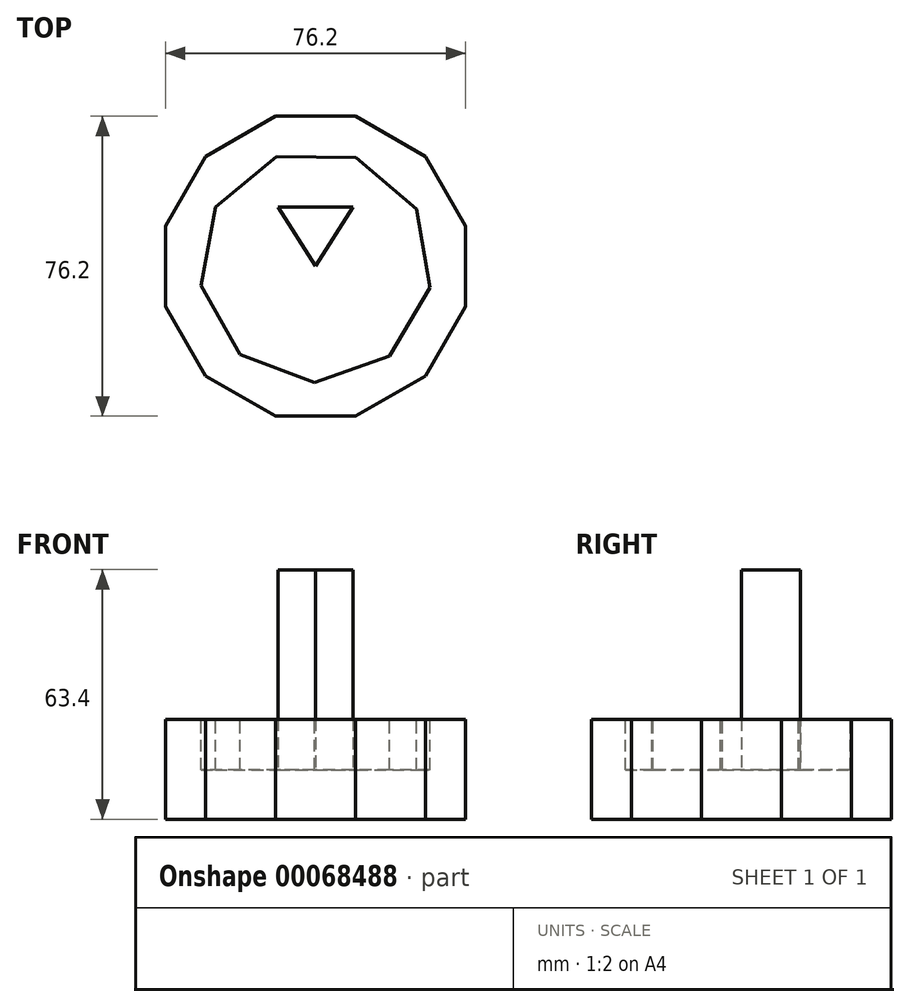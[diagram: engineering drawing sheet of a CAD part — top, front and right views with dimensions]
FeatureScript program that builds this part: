
annotation { "Feature Type Name" : "Feature", "Feature Type Description" : "" }
export const myFeature = defineFeature(function(context is Context, id is Id, definition is map)
    precondition{}
    {
        {
            var Q0;
            Q0=qCreatedBy(makeId("Top.planeOp"),FACE);
            var sketch = newSketch(context, id + "F0", { "sketchPlane" : qUnion([Q0])});
            skCircle(sketch, "E0.cCircle", {"center": v(0, 0) * mm, "radius": 38.1 * mm, "construction": true});
            skLineSegment(sketch, "E0.0", {"start": v(38.1, 10.2) * mm, "end": v(38.1, -10.2) * mm});
            skLineSegment(sketch, "E0.1", {"start": v(38.1, -10.2) * mm, "end": v(27.9, -27.9) * mm});
            skLineSegment(sketch, "E0.2", {"start": v(27.9, -27.9) * mm, "end": v(10.2, -38.1) * mm});
            skLineSegment(sketch, "E0.3", {"start": v(10.2, -38.1) * mm, "end": v(-10.2, -38.1) * mm});
            skLineSegment(sketch, "E0.4", {"start": v(-10.2, -38.1) * mm, "end": v(-27.9, -27.9) * mm});
            skLineSegment(sketch, "E0.5", {"start": v(-27.9, -27.9) * mm, "end": v(-38.1, -10.2) * mm});
            skLineSegment(sketch, "E0.6", {"start": v(-38.1, -10.2) * mm, "end": v(-38.1, 10.2) * mm});
            skLineSegment(sketch, "E0.7", {"start": v(-38.1, 10.2) * mm, "end": v(-27.9, 27.9) * mm});
            skLineSegment(sketch, "E0.8", {"start": v(-27.9, 27.9) * mm, "end": v(-10.2, 38.1) * mm});
            skLineSegment(sketch, "E0.9", {"start": v(-10.2, 38.1) * mm, "end": v(10.2, 38.1) * mm});
            skLineSegment(sketch, "E0.10", {"start": v(10.2, 38.1) * mm, "end": v(27.9, 27.9) * mm});
            skLineSegment(sketch, "E0.11", {"start": v(27.9, 27.9) * mm, "end": v(38.1, 10.2) * mm});
            skPoint(sketch, "E0.0.midPoint", {"position": v(38.1, 0) * mm});
            skSolve(sketch);
        }
        {
            var Q0;
            Q0 = qSketchRegion(id + "F0", true);
            extrude(context, id + "F1", {"entities" : qUnion([Q0]), "depth" : 25.4 * mm});
        }
        {
            var Q0;
            Q0=makeQuery(id+"F1.opExtrude","CAP_FACE",FACE,{"disambiguationData":[OSD([sQuery(id+"F0.wireOp",EDGE,"E0.0"),sQuery(id+"F0.wireOp",EDGE,"E0.1"),sQuery(id+"F0.wireOp",EDGE,"E0.2"),sQuery(id+"F0.wireOp",EDGE,"E0.3"),sQuery(id+"F0.wireOp",EDGE,"E0.4"),sQuery(id+"F0.wireOp",EDGE,"E0.5"),sQuery(id+"F0.wireOp",EDGE,"E0.6"),sQuery(id+"F0.wireOp",EDGE,"E0.7"),sQuery(id+"F0.wireOp",EDGE,"E0.8"),sQuery(id+"F0.wireOp",EDGE,"E0.9"),sQuery(id+"F0.wireOp",EDGE,"E0.10"),sQuery(id+"F0.wireOp",EDGE,"E0.11")])],"isStart":false});
            var sketch = newSketch(context, id + "F2", { "sketchPlane" : qUnion([Q0])});
            skCircle(sketch, "E1.cCircle", {"center": v(0, 0) * mm, "radius": 27.74 * mm, "construction": true});
            skLineSegment(sketch, "E1.0", {"start": v(29.03, -5.37) * mm, "end": v(18.79, -22.78) * mm});
            skLineSegment(sketch, "E1.1", {"start": v(18.79, -22.78) * mm, "end": v(-0.25, -29.52) * mm});
            skLineSegment(sketch, "E1.2", {"start": v(-0.25, -29.52) * mm, "end": v(-19.17, -22.46) * mm});
            skLineSegment(sketch, "E1.3", {"start": v(-19.17, -22.46) * mm, "end": v(-29.12, -4.88) * mm});
            skLineSegment(sketch, "E1.4", {"start": v(-29.12, -4.88) * mm, "end": v(-25.44, 14.98) * mm});
            skLineSegment(sketch, "E1.5", {"start": v(-25.44, 14.98) * mm, "end": v(-9.86, 27.83) * mm});
            skLineSegment(sketch, "E1.6", {"start": v(-9.86, 27.83) * mm, "end": v(10.33, 27.66) * mm});
            skLineSegment(sketch, "E1.7", {"start": v(10.33, 27.66) * mm, "end": v(25.7, 14.55) * mm});
            skLineSegment(sketch, "E1.8", {"start": v(25.7, 14.55) * mm, "end": v(29.03, -5.37) * mm});
            skPoint(sketch, "E1.0.midPoint", {"position": v(23.9, -14.07) * mm});
            skSolve(sketch);
        }
        {
            var Q0;
            Q0=makeQuery(id+"F2.imprint","IMPRINT",FACE,{"disambiguationData":[TD([[makeQuery(id+"F2.imprint","IMPRINT",EDGE,{"derivedFrom":sQuery(id+"F2.wireOp",EDGE,"E1.0")}),-1.0]])]});
            extrude(context, id + "F3", {"entities" : qUnion([Q0]), "operationType" : NewBodyOperationType.REMOVE, "oppositeDirection" : true, "depth" : 12.8 * mm});
        }
        {
            var Q0;
            Q0=makeQuery(id+"F3.boolean.opBoolean","COPY",FACE,{"derivedFrom":makeQuery(id+"F3.opExtrude","CAP_FACE",FACE,{"disambiguationData":[OSD([sQuery(id+"F2.wireOp",EDGE,"E1.0"),sQuery(id+"F2.wireOp",EDGE,"E1.1"),sQuery(id+"F2.wireOp",EDGE,"E1.2"),sQuery(id+"F2.wireOp",EDGE,"E1.3"),sQuery(id+"F2.wireOp",EDGE,"E1.4"),sQuery(id+"F2.wireOp",EDGE,"E1.5"),sQuery(id+"F2.wireOp",EDGE,"E1.6"),sQuery(id+"F2.wireOp",EDGE,"E1.7"),sQuery(id+"F2.wireOp",EDGE,"E1.8")])],"isStart":false})});
            var sketch = newSketch(context, id + "F4", { "sketchPlane" : qUnion([Q0])});
            skLineSegment(sketch, "E2", {"start": v(0, 0) * mm, "end": v(9.54, 14.98) * mm});
            skLineSegment(sketch, "E3", {"start": v(9.54, 14.98) * mm, "end": v(-9.54, 14.98) * mm});
            skLineSegment(sketch, "E4", {"start": v(-9.54, 14.98) * mm, "end": v(0, 0) * mm});
            skSolve(sketch);
        }
        {
            var Q0;
            Q0 = qSketchRegion(id + "F4", true);
            extrude(context, id + "F5", {"entities" : qUnion([Q0]), "operationType" : NewBodyOperationType.ADD, "depth" : 50.8 * mm});
        }
    });
